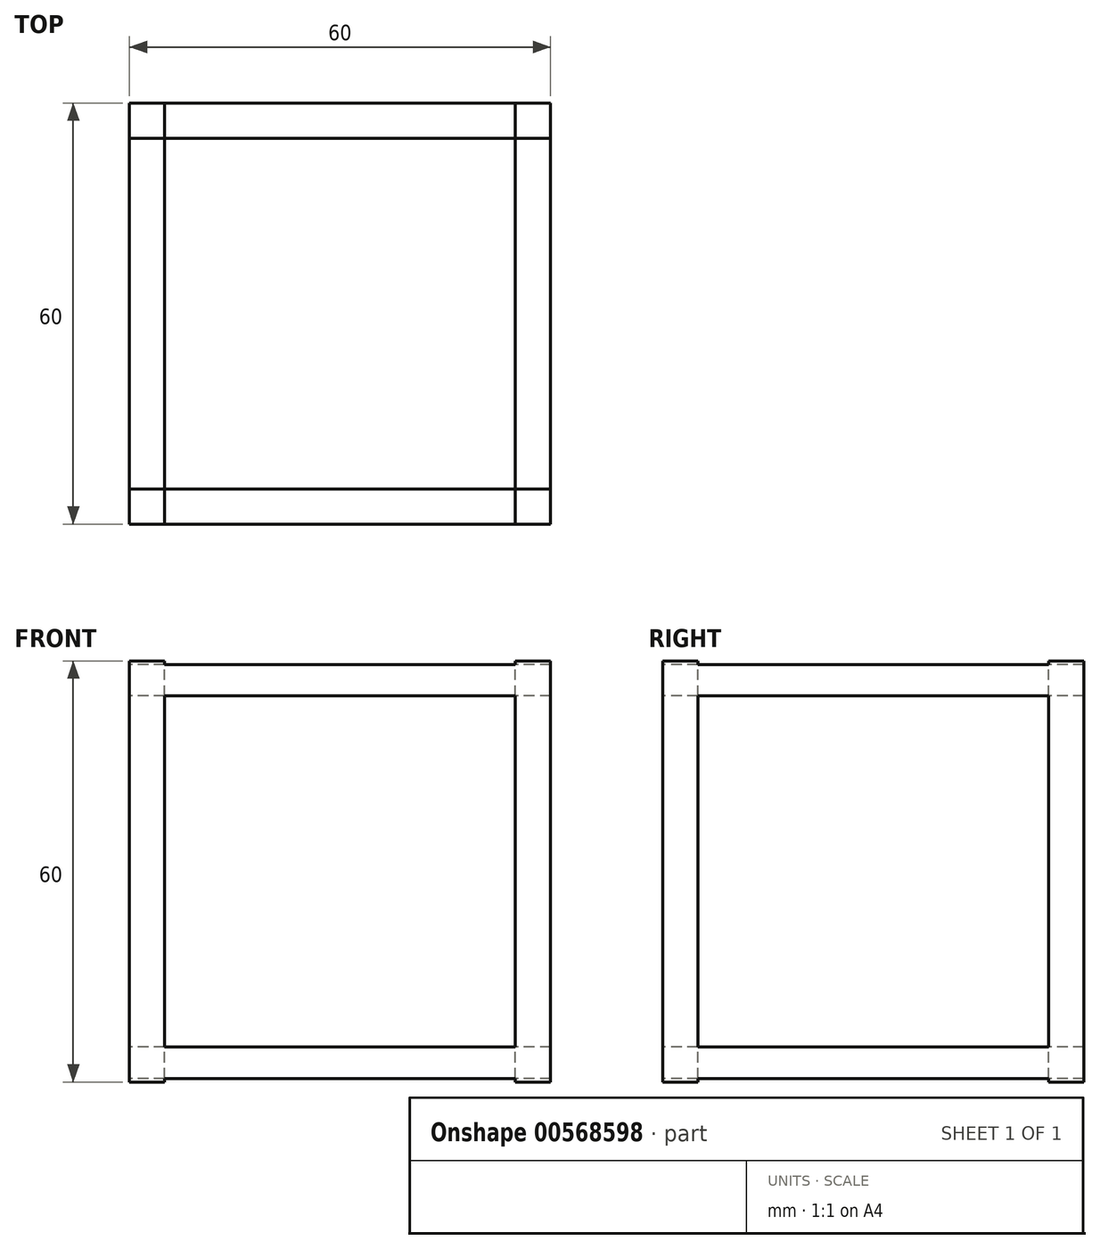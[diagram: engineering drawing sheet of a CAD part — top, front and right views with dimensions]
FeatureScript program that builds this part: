
annotation { "Feature Type Name" : "Feature", "Feature Type Description" : "" }
export const myFeature = defineFeature(function(context is Context, id is Id, definition is map)
    precondition{}
    {
        {
            var Q0;
            Q0=qCreatedBy(makeId("Right.planeOp"),FACE);
            var sketch = newSketch(context, id + "F0", { "sketchPlane" : qUnion([Q0])});
            skLineSegment(sketch, "E0", {"start": v(5, 59.5) * mm, "end": v(55, 59.5) * mm});
            skLineSegment(sketch, "E1", {"start": v(55, 59.5) * mm, "end": v(55, 60) * mm});
            skLineSegment(sketch, "E2", {"start": v(55, 60) * mm, "end": v(60, 60) * mm});
            skLineSegment(sketch, "E3", {"start": v(60, 60) * mm, "end": v(60, 0) * mm});
            skLineSegment(sketch, "E4", {"start": v(60, 0) * mm, "end": v(55, 0) * mm});
            skLineSegment(sketch, "E5", {"start": v(55, 0) * mm, "end": v(55, 0.5) * mm});
            skLineSegment(sketch, "E6", {"start": v(55, 0.5) * mm, "end": v(5, 0.5) * mm});
            skLineSegment(sketch, "E7", {"start": v(5, 0.5) * mm, "end": v(5, 0) * mm});
            skLineSegment(sketch, "E8", {"start": v(5, 0) * mm, "end": v(0, 0) * mm});
            skLineSegment(sketch, "E9", {"start": v(0, 0) * mm, "end": v(0, 60) * mm});
            skLineSegment(sketch, "E10", {"start": v(0, 60) * mm, "end": v(5, 60) * mm});
            skLineSegment(sketch, "E11", {"start": v(5, 60) * mm, "end": v(5, 59.5) * mm});
            skLineSegment(sketch, "E12.bottom", {"start": v(55, 55) * mm, "end": v(5, 55) * mm});
            skLineSegment(sketch, "E12.top", {"start": v(55, 5) * mm, "end": v(5, 5) * mm});
            skLineSegment(sketch, "E12.left", {"start": v(55, 55) * mm, "end": v(55, 5) * mm});
            skLineSegment(sketch, "E12.right", {"start": v(5, 55) * mm, "end": v(5, 5) * mm});
            skSolve(sketch);
        }
        {
            var Q0;
            Q0 = qSketchRegion(id + "F0", true);
            extrude(context, id + "F1", {"entities" : qUnion([Q0]), "depth" : 60 * mm, "offsetDistance" : 25 * mm});
        }
        {
            var Q0;
            Q0=makeQuery(id+"F1.opExtrude","SWEPT_FACE",FACE,{"disambiguationData":[OSD([sQuery(id+"F0.wireOp",EDGE,"E9")])]});
            var sketch = newSketch(context, id + "F2", { "sketchPlane" : qUnion([Q0])});
            skLineSegment(sketch, "E13.bottom", {"start": v(5, 59.5) * mm, "end": v(55, 59.5) * mm});
            skLineSegment(sketch, "E13.top", {"start": v(5, 0.5) * mm, "end": v(55, 0.5) * mm});
            skLineSegment(sketch, "E13.left", {"start": v(5, 59.5) * mm, "end": v(5, 0.5) * mm});
            skLineSegment(sketch, "E13.right", {"start": v(55, 59.5) * mm, "end": v(55, 0.5) * mm});
            skLineSegment(sketch, "E14.bottom", {"start": v(5, 55) * mm, "end": v(55, 55) * mm});
            skLineSegment(sketch, "E14.top", {"start": v(5, 5) * mm, "end": v(55, 5) * mm});
            skLineSegment(sketch, "E14.left", {"start": v(5, 55) * mm, "end": v(5, 5) * mm});
            skLineSegment(sketch, "E14.right", {"start": v(55, 55) * mm, "end": v(55, 5) * mm});
            skLineSegment(sketch, "E15.top", {"start": v(5, 75) * mm, "end": v(55, 75) * mm});
            skLineSegment(sketch, "E15.left", {"start": v(5, 59.5) * mm, "end": v(5, 75) * mm});
            skLineSegment(sketch, "E15.right", {"start": v(55, 59.5) * mm, "end": v(55, 75) * mm});
            skLineSegment(sketch, "E16.top", {"start": v(5, -19.5) * mm, "end": v(55, -19.5) * mm});
            skLineSegment(sketch, "E16.left", {"start": v(5, 0.5) * mm, "end": v(5, -19.5) * mm});
            skLineSegment(sketch, "E16.right", {"start": v(55, 0.5) * mm, "end": v(55, -19.5) * mm});
            skSolve(sketch);
        }
        {
            var Q0;
            Q0 = qSketchRegion(id + "F0", true);
            extrude(context, id + "F3", {"entities" : qUnion([Q0]), "operationType" : NewBodyOperationType.ADD, "depth" : 60 * mm, "offsetDistance" : 25 * mm});
        }
        {
            var Q0;
            Q0=makeQuery(id+"F2.imprint","IMPRINT",FACE,{"disambiguationData":[TD([[makeQuery(id+"F2.imprint","IMPRINT",EDGE,{"derivedFrom":sQuery(id+"F2.wireOp",EDGE,"E14.bottom")}),-1.0]])]});
            var Q1;
            {var subQ0=sQuery(id+"F2.wireOp",EDGE,"E16.top");Q1=makeQuery(id+"F2.imprint","IMPRINT",FACE,{"disambiguationData":[TD([[makeQuery(id+"F2.imprint","IMPRINT",EDGE,{"derivedFrom":subQ0}),1.0]])]});}
            var Q2;
            {var subQ0=sQuery(id+"F2.wireOp",EDGE,"E13.bottom");Q2=makeQuery(id+"F2.imprint","IMPRINT",FACE,{"disambiguationData":[TD([[makeQuery(id+"F2.imprint","IMPRINT",EDGE,{"derivedFrom":subQ0}),1.0]])]});}
            var Q3;
            {var subQ0=sQuery(id+"F2.wireOp",EDGE,"E13.top");Q3=makeQuery(id+"F2.imprint","IMPRINT",FACE,{"disambiguationData":[TD([[makeQuery(id+"F2.imprint","IMPRINT",EDGE,{"derivedFrom":subQ0}),-1.0]])]});}
            var Q4;
            {var subQ0=sQuery(id+"F2.wireOp",EDGE,"E15.top");Q4=makeQuery(id+"F2.imprint","IMPRINT",FACE,{"disambiguationData":[TD([[makeQuery(id+"F2.imprint","IMPRINT",EDGE,{"derivedFrom":subQ0}),-1.0]])]});}
            extrude(context, id + "F4", {"entities" : qUnion([Q0, Q1, Q2, Q3, Q4]), "operationType" : NewBodyOperationType.REMOVE, "oppositeDirection" : true, "depth" : 60 * mm, "offsetDistance" : 25 * mm});
        }
        {
            var Q0;
            {var subQ1=sQuery(id+"F0.wireOp",EDGE,"E2");Q0=makeQuery(id+"F4.boolean.opBoolean","SPLIT",FACE,{"disambiguationData":[TD([makeQuery(id+"F4.opExtrude","SWEPT_FACE",FACE,{"disambiguationData":[OSD([sQuery(id+"F2.wireOp",EDGE,"E15.left")])]})])],"derivedFrom":makeQuery(id+"F1.opExtrude","SWEPT_FACE",FACE,{"disambiguationData":[OSD([subQ1])]})});}
            cPlane(context, id + "F5", {"entities" : qUnion([Q0]), "cplaneType" : CPlaneType.OFFSET, "offset" : 0 * mm, "width" : 150 * mm, "height" : 150 * mm});
        }
        {
            var Q0;
            Q0=qCreatedBy(id+"F5.planeOp",FACE);
            var sketch = newSketch(context, id + "F6", { "sketchPlane" : qUnion([Q0])});
            skLineSegment(sketch, "E17.bottom", {"start": v(5, 55) * mm, "end": v(55, 55) * mm});
            skLineSegment(sketch, "E17.top", {"start": v(5, 5) * mm, "end": v(55, 5) * mm});
            skLineSegment(sketch, "E17.left", {"start": v(5, 55) * mm, "end": v(5, 5) * mm});
            skLineSegment(sketch, "E17.right", {"start": v(55, 55) * mm, "end": v(55, 5) * mm});
            skSolve(sketch);
        }
        {
            var Q0;
            Q0 = qSketchRegion(id + "F6", true);
            extrude(context, id + "F7", {"entities" : qUnion([Q0]), "operationType" : NewBodyOperationType.REMOVE, "oppositeDirection" : true, "depth" : 60 * mm, "offsetDistance" : 25 * mm});
        }
    });
